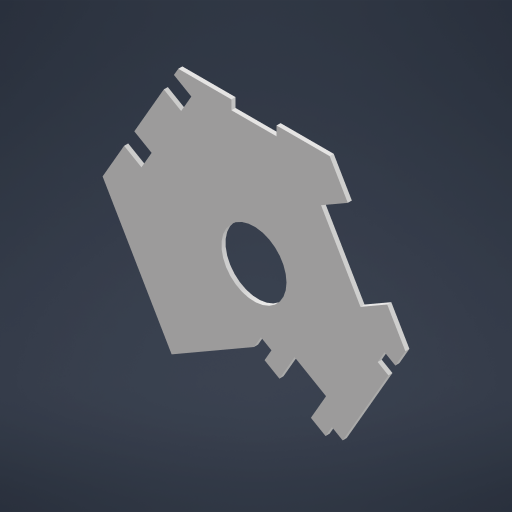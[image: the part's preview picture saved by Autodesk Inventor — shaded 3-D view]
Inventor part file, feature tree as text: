
AUTODESK INVENTOR PART (.ipt)
format: ipt  version: 2023 (Build 270158000, 158)  size: 233,984 bytes
history: native  units: in
note: dims shown in document units (in); Inventor stores cm internally (conversion verified against a paired STEP export)
features: extrude x1, sketch x1
ambient origin geometry x8: Origin, YZ Plane, XZ Plane, XY Plane, X Axis, Y Axis, Z Axis, Center Point
bodies: Solid1 (feature_tree)
feature tree (2):
  extrude  "Extrusion1"  Depth=0.0394in
  sketch  "Sketch1"  dims[d0=2.5394in d1=0.1287in d2=0.0394in d3=0.6299in d4=0.4626in d5=0.1937in d6=0.1969in d7=0.5709in d8=0.1945in d9=0.1969in d10=0.2185in d11=0.2185in d12=0.0909in d13=0.3819in d14=0.3819in d15=0.2992in d16=0.1949in d17=0.1201in d18=0.1339in d19=0.8858in d21=0.1205in d22=0.176in d23=0.176in d24=0.2937in d25=0.1661in d26=0.1339in d27=0.0394in d28=0.0in]
